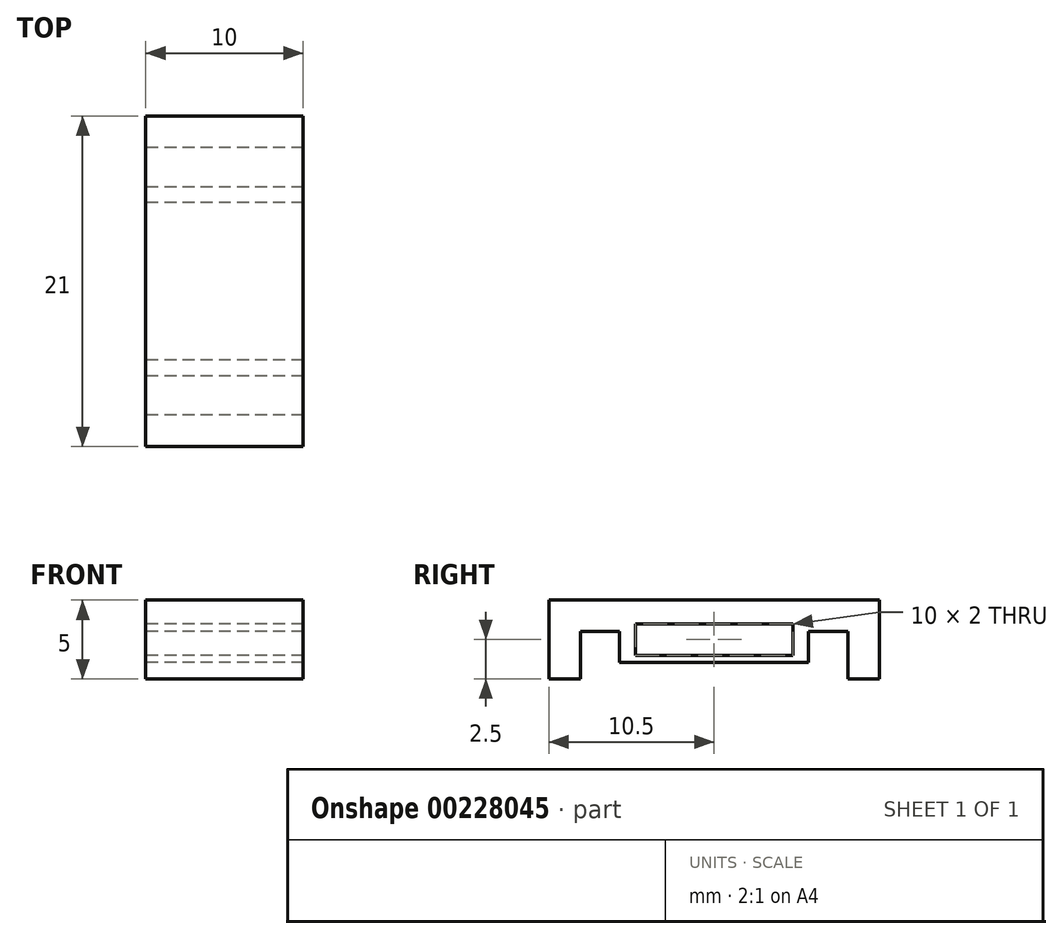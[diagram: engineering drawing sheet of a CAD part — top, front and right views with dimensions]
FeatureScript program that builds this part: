
annotation { "Feature Type Name" : "Feature", "Feature Type Description" : "" }
export const myFeature = defineFeature(function(context is Context, id is Id, definition is map)
    precondition{}
    {
        {
            var Q0;
            Q0=qCreatedBy(makeId("Right.planeOp"),FACE);
            var sketch = newSketch(context, id + "F0", { "sketchPlane" : qUnion([Q0])});
            skLineSegment(sketch, "E0.bottom", {"start": v(10.5, 2.5) * mm, "end": v(-10.5, 2.5) * mm});
            skLineSegment(sketch, "E0.left", {"start": v(10.5, 2.5) * mm, "end": v(10.5, -2.5) * mm});
            skLineSegment(sketch, "E0.right", {"start": v(-10.5, 2.5) * mm, "end": v(-10.5, -2.5) * mm});
            skPoint(sketch, "E0.middle", {"position": v(0, 0) * mm});
            skLineSegment(sketch, "E1.0", {"start": v(-8.5, 0.5) * mm, "end": v(-8.5, -2.5) * mm});
            skLineSegment(sketch, "E1.1", {"start": v(8.5, 0.5) * mm, "end": v(6, 0.5) * mm});
            skLineSegment(sketch, "E1.2", {"start": v(8.5, 0.5) * mm, "end": v(8.5, -2.5) * mm});
            skLineSegment(sketch, "E2", {"start": v(-10.5, -2.5) * mm, "end": v(-8.5, -2.5) * mm});
            skLineSegment(sketch, "E3", {"start": v(8.5, -2.5) * mm, "end": v(10.5, -2.5) * mm});
            skLineSegment(sketch, "E4.bottom", {"start": v(6, -1.46) * mm, "end": v(-6, -1.46) * mm});
            skLineSegment(sketch, "E4.top", {"start": v(6, 1.46) * mm, "end": v(-6, 1.46) * mm});
            skLineSegment(sketch, "E4.left", {"start": v(6, -1.46) * mm, "end": v(6, 1.46) * mm});
            skLineSegment(sketch, "E4.right", {"start": v(-6, -1.46) * mm, "end": v(-6, 1.46) * mm});
            skLineSegment(sketch, "E5.trimOffspring", {"start": v(-6, 0.5) * mm, "end": v(-8.5, 0.5) * mm});
            skLineSegment(sketch, "E6.bottom", {"start": v(5, 1) * mm, "end": v(-5, 1) * mm});
            skLineSegment(sketch, "E6.top", {"start": v(5, -1) * mm, "end": v(-5, -1) * mm});
            skLineSegment(sketch, "E6.left", {"start": v(5, 1) * mm, "end": v(5, -1) * mm});
            skLineSegment(sketch, "E6.right", {"start": v(-5, 1) * mm, "end": v(-5, -1) * mm});
            skSolve(sketch);
        }
        {
            var Q0;
            Q0=makeQuery(id+"F0.imprint","IMPRINT",FACE,{"disambiguationData":[TD([[makeQuery(id+"F0.imprint","IMPRINT",EDGE,{"derivedFrom":sQuery(id+"F0.wireOp",EDGE,"E0.bottom")}),1.0]])]});
            var Q1;
            {var subQ3=sQuery(id+"F0.wireOp",EDGE,"E4.bottom");Q1=makeQuery(id+"F0.imprint","IMPRINT",FACE,{"disambiguationData":[TD([[makeQuery(id+"F0.imprint","IMPRINT",EDGE,{"derivedFrom":subQ3}),-1.0]])]});}
            extrude(context, id + "F1", {"entities" : qUnion([Q0, Q1]), "depth" : 10 * mm});
        }
    });
